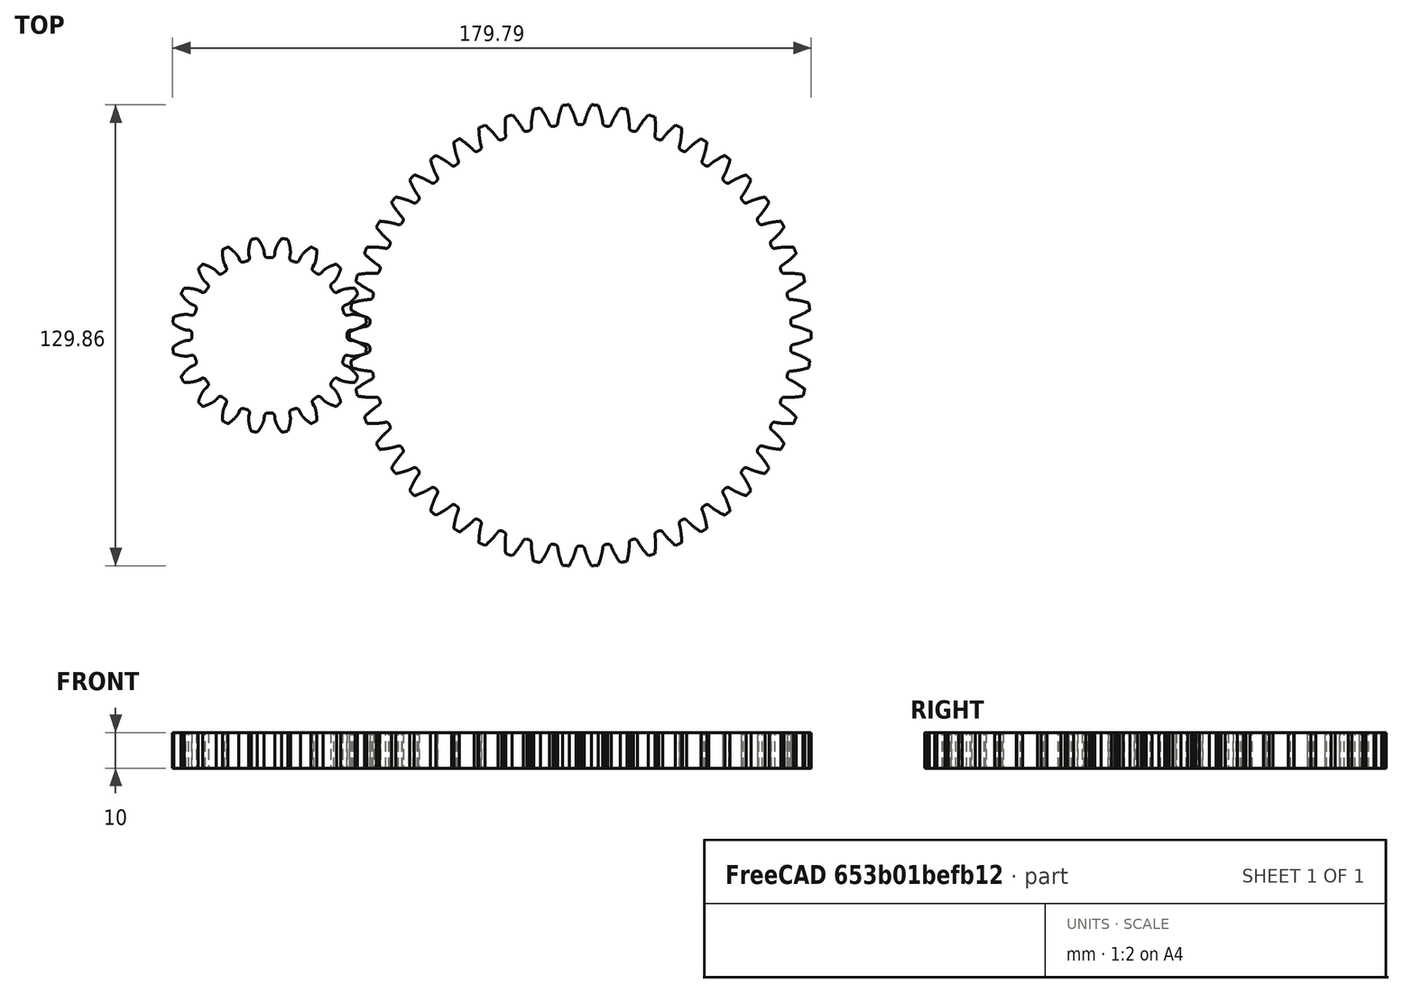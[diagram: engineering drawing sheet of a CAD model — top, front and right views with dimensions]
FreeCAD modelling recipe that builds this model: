
FCSTD DOCUMENT  (FreeCAD 0.20R29177 +426 (Git))
Label: 14_-Tren_de_enranajes__z20_z50
License: All rights reserved
LicenseURL: http://en.wikipedia.org/wiki/All_rights_reserved
objects: Part::Part2DObjectPython×2, PartDesign::Pad×2, PartDesign::Body×2
note: 8 computed .brp shape members not serialized (recipe doc carries the construction recipe); baked Part::Feature solids carry a one-line shape summary decoded from their .brp

FEATURE [Part::Part2DObjectPython] InvoluteGear  # Draft 2D object (typed FeaturePython)
  ExternalGear = true
  HighPrecision = true
  Modules = 2.5
  NumberOfTeeth = 20
  PressureAngle = 20
FEATURE [PartDesign::Pad] Pad
  Direction = (0,0,1)
  Length = 10
  Length2 = 10
  Profile = -> InvoluteGear
  ReferenceAxis = -> InvoluteGear [N_Axis]
  Type = 0
FEATURE [PartDesign::Body] Body  label="Engranaje 1"
  Group = -> [InvoluteGear,Pad]
  Origin = -> Origin
  Placement = pos=(0,0,0) rot=(0,0,1;-24.0332rad)
  Tip = -> Pad
FEATURE [Part::Part2DObjectPython] InvoluteGear001  # Draft 2D object (typed FeaturePython)
  ExternalGear = true
  HighPrecision = true
  Modules = 2.5
  NumberOfTeeth = 50
  PressureAngle = 20
FEATURE [PartDesign::Pad] Pad001
  Direction = (0,0,1)
  Length = 10
  Length2 = 10
  Profile = -> InvoluteGear001
  ReferenceAxis = -> InvoluteGear001 [N_Axis]
  Type = 0
FEATURE [PartDesign::Body] Body001  label="Engranaje 2 "
  Group = -> [InvoluteGear001,Pad001]
  Origin = -> Origin001
  Placement = pos=(87.5,0,0) rot=(0,0,1;9.6761rad)
  Tip = -> Pad001
